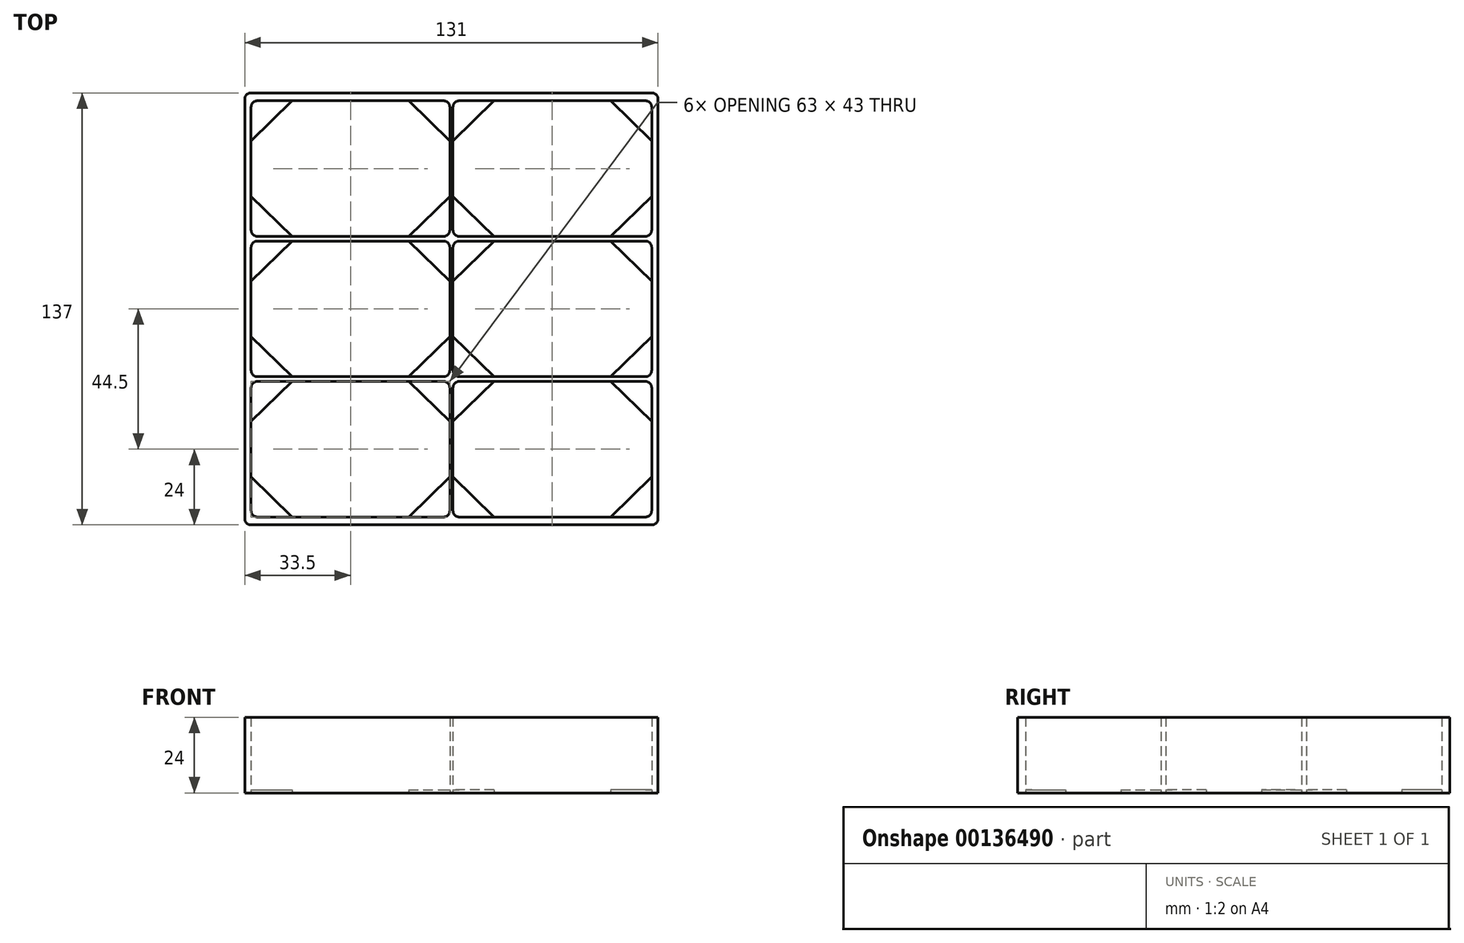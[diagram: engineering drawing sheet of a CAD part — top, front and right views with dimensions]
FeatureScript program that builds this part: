
annotation { "Feature Type Name" : "Feature", "Feature Type Description" : "" }
export const myFeature = defineFeature(function(context is Context, id is Id, definition is map)
    precondition{}
    {
        {
            var Q0;
            Q0=qCreatedBy(makeId("Top.planeOp"),FACE);
            var sketch = newSketch(context, id + "F0", { "sketchPlane" : qUnion([Q0])});
            skLineSegment(sketch, "E0.bottom", {"start": v(65.5, 68.5) * mm, "end": v(-65.5, 68.5) * mm});
            skLineSegment(sketch, "E0.top", {"start": v(65.5, -68.5) * mm, "end": v(-65.5, -68.5) * mm});
            skLineSegment(sketch, "E0.left", {"start": v(65.5, 68.5) * mm, "end": v(65.5, -68.5) * mm});
            skLineSegment(sketch, "E0.right", {"start": v(-65.5, 68.5) * mm, "end": v(-65.5, -68.5) * mm});
            skPoint(sketch, "E0.middle", {"position": v(0, 0) * mm});
            skLineSegment(sketch, "E1.bottom", {"start": v(63.5, -66) * mm, "end": v(-63.5, -66) * mm});
            skLineSegment(sketch, "E1.top", {"start": v(63.5, 66) * mm, "end": v(-63.5, 66) * mm});
            skLineSegment(sketch, "E1.left", {"start": v(63.5, -66) * mm, "end": v(63.5, 66) * mm});
            skLineSegment(sketch, "E1.right", {"start": v(-63.5, -66) * mm, "end": v(-63.5, 66) * mm});
            skLineSegment(sketch, "E2", {"start": v(-0.5, 66) * mm, "end": v(-0.5, -66) * mm});
            skPoint(sketch, "E2.endSnap0", {"position": v(0, -66) * mm});
            skLineSegment(sketch, "E3", {"start": v(-63.5, 23) * mm, "end": v(-0.5, 23) * mm});
            skLineSegment(sketch, "E4", {"start": v(-0.5, 21.5) * mm, "end": v(-63.5, 21.5) * mm});
            skLineSegment(sketch, "E5.MirrorCS", {"start": v(-63.5, -23) * mm, "end": v(-0.5, -23) * mm});
            skLineSegment(sketch, "E6.MirrorCS", {"start": v(-0.5, -21.5) * mm, "end": v(-63.5, -21.5) * mm});
            skLineSegment(sketch, "E7.MirrorCS", {"start": v(0.5, 66) * mm, "end": v(0.5, -66) * mm});
            skLineSegment(sketch, "E8.MirrorCS", {"start": v(63.5, 23) * mm, "end": v(0.5, 23) * mm});
            skLineSegment(sketch, "E9.MirrorCS", {"start": v(0.5, 21.5) * mm, "end": v(63.5, 21.5) * mm});
            skLineSegment(sketch, "E10.MirrorCS", {"start": v(0.5, -21.5) * mm, "end": v(63.5, -21.5) * mm});
            skLineSegment(sketch, "E11.MirrorCS", {"start": v(63.5, -23) * mm, "end": v(0.5, -23) * mm});
            skLineSegment(sketch, "E12", {"start": v(-63.5, 53.26) * mm, "end": v(-50.5, 66) * mm});
            skLineSegment(sketch, "E13.MirrorCS", {"start": v(63.5, 53.26) * mm, "end": v(50.5, 66) * mm});
            skLineSegment(sketch, "E14.MirrorCS", {"start": v(-63.5, -53.26) * mm, "end": v(-50.5, -66) * mm});
            skLineSegment(sketch, "E15.MirrorCS", {"start": v(63.5, -53.26) * mm, "end": v(50.5, -66) * mm});
            skLineSegment(sketch, "E16", {"start": v(-13.5, 66) * mm, "end": v(-0.5, 53.26) * mm});
            skLineSegment(sketch, "E17.MirrorCS", {"start": v(13.5, 66) * mm, "end": v(0.5, 53.26) * mm});
            skLineSegment(sketch, "E18.MirrorCS", {"start": v(-13.5, -66) * mm, "end": v(-0.5, -53.26) * mm});
            skLineSegment(sketch, "E19.MirrorCS", {"start": v(13.5, -66) * mm, "end": v(0.5, -53.26) * mm});
            skLineSegment(sketch, "E20", {"start": v(-63.5, 44.5) * mm, "end": v(63.5, 44.5) * mm, "construction": true});
            skLineSegment(sketch, "E21.MirrorCS", {"start": v(-13.5, 23) * mm, "end": v(-0.5, 35.74) * mm});
            skLineSegment(sketch, "E22.MirrorCS", {"start": v(-63.5, 35.74) * mm, "end": v(-50.5, 23) * mm});
            skLineSegment(sketch, "E23.MirrorCS", {"start": v(13.5, 23) * mm, "end": v(0.5, 35.74) * mm});
            skLineSegment(sketch, "E24.MirrorCS", {"start": v(63.5, 35.74) * mm, "end": v(50.5, 23) * mm});
            skLineSegment(sketch, "E25", {"start": v(63.5, 22.25) * mm, "end": v(-63.5, 22.25) * mm, "construction": true});
            skLineSegment(sketch, "E26.MirrorCS", {"start": v(-63.5, 8.76) * mm, "end": v(-50.5, 21.5) * mm});
            skLineSegment(sketch, "E27.MirrorCS", {"start": v(-63.5, -8.76) * mm, "end": v(-50.5, -21.5) * mm});
            skLineSegment(sketch, "E28.MirrorCS", {"start": v(-13.5, -21.5) * mm, "end": v(-0.5, -8.76) * mm});
            skLineSegment(sketch, "E29.MirrorCS", {"start": v(-13.5, 21.5) * mm, "end": v(-0.5, 8.76) * mm});
            skLineSegment(sketch, "E30.MirrorCS", {"start": v(13.5, 21.5) * mm, "end": v(0.5, 8.76) * mm});
            skLineSegment(sketch, "E31.MirrorCS", {"start": v(13.5, -21.5) * mm, "end": v(0.5, -8.76) * mm});
            skLineSegment(sketch, "E32.MirrorCS", {"start": v(63.5, -8.76) * mm, "end": v(50.5, -21.5) * mm});
            skLineSegment(sketch, "E33.MirrorCS", {"start": v(63.5, 8.76) * mm, "end": v(50.5, 21.5) * mm});
            skLineSegment(sketch, "E34.MirrorCS", {"start": v(-13.5, -23) * mm, "end": v(-0.5, -35.74) * mm});
            skLineSegment(sketch, "E35.MirrorCS", {"start": v(-63.5, -35.74) * mm, "end": v(-50.5, -23) * mm});
            skLineSegment(sketch, "E36.MirrorCS", {"start": v(13.5, -23) * mm, "end": v(0.5, -35.74) * mm});
            skLineSegment(sketch, "E37.MirrorCS", {"start": v(63.5, -35.74) * mm, "end": v(50.5, -23) * mm});
            skSolve(sketch);
        }
        {
            var Q0;
            Q0=makeQuery(id+"F0.imprint","IMPRINT",FACE,{"disambiguationData":[TD([[makeQuery(id+"F0.imprint","IMPRINT",EDGE,{"derivedFrom":sQuery(id+"F0.wireOp",EDGE,"E0.bottom")}),1.0]])]});
            var Q1;
            {var subQ12=sQuery(id+"F0.wireOp",EDGE,"E2");var subQ20=sQuery(id+"F0.wireOp",EDGE,"E1.bottom");var subQ21=makeQuery(id+"F0.imprint","INTERSECT",VERTEX,{"derivedFrom":[subQ20,subQ12]});Q1=makeQuery(id+"F0.imprint","IMPRINT",FACE,{"disambiguationData":[TD([[makeQuery(id+"F0.imprint","IMPRINT",EDGE,{"disambiguationData":[TD([[subQ21,1.0]])],"derivedFrom":subQ20}),-1.0]])]});}
            var Q2;
            {var subQ0=sQuery(id+"F0.wireOp",EDGE,"E8.MirrorCS");var subQ3=sQuery(id+"F0.wireOp",EDGE,"E1.left");var subQ4=makeQuery(id+"F0.imprint","INTERSECT",VERTEX,{"derivedFrom":[subQ3,subQ0]});Q2=makeQuery(id+"F0.imprint","IMPRINT",FACE,{"disambiguationData":[TD([[makeQuery(id+"F0.imprint","IMPRINT",EDGE,{"disambiguationData":[TD([[subQ4,1.0]])],"derivedFrom":subQ3}),1.0]])]});}
            var Q3;
            {var subQ0=sQuery(id+"F0.wireOp",EDGE,"E3");var subQ5=sQuery(id+"F0.wireOp",EDGE,"E1.right");var subQ6=makeQuery(id+"F0.imprint","INTERSECT",VERTEX,{"derivedFrom":[subQ5,subQ0]});Q3=makeQuery(id+"F0.imprint","IMPRINT",FACE,{"disambiguationData":[TD([[makeQuery(id+"F0.imprint","IMPRINT",EDGE,{"disambiguationData":[TD([[subQ6,1.0]])],"derivedFrom":subQ5}),-1.0]])]});}
            var Q4;
            {var subQ0=sQuery(id+"F0.wireOp",EDGE,"E5.MirrorCS");var subQ3=sQuery(id+"F0.wireOp",EDGE,"E1.right");var subQ4=makeQuery(id+"F0.imprint","INTERSECT",VERTEX,{"derivedFrom":[subQ3,subQ0]});Q4=makeQuery(id+"F0.imprint","IMPRINT",FACE,{"disambiguationData":[TD([[makeQuery(id+"F0.imprint","IMPRINT",EDGE,{"disambiguationData":[TD([[subQ4,-1.0]])],"derivedFrom":subQ3}),-1.0]])]});}
            var Q5;
            {var subQ0=sQuery(id+"F0.wireOp",EDGE,"E10.MirrorCS");var subQ7=sQuery(id+"F0.wireOp",EDGE,"E1.left");var subQ8=makeQuery(id+"F0.imprint","INTERSECT",VERTEX,{"derivedFrom":[subQ7,subQ0]});Q5=makeQuery(id+"F0.imprint","IMPRINT",FACE,{"disambiguationData":[TD([[makeQuery(id+"F0.imprint","IMPRINT",EDGE,{"disambiguationData":[TD([[subQ8,1.0]])],"derivedFrom":subQ7}),1.0]])]});}
            extrude(context, id + "F1", {"entities" : qUnion([Q0, Q1, Q2, Q3, Q4, Q5]), "depth" : 24 * mm});
        }
        {
            var Q0;
            {var subQ3=sQuery(id+"F0.wireOp",EDGE,"E12");Q0=makeQuery(id+"F0.imprint","IMPRINT",FACE,{"disambiguationData":[TD([[makeQuery(id+"F0.imprint","IMPRINT",EDGE,{"derivedFrom":subQ3}),1.0]])]});}
            var Q1;
            {var subQ3=sQuery(id+"F0.wireOp",EDGE,"E22.MirrorCS");Q1=makeQuery(id+"F0.imprint","IMPRINT",FACE,{"disambiguationData":[TD([[makeQuery(id+"F0.imprint","IMPRINT",EDGE,{"derivedFrom":subQ3}),-1.0]])]});}
            var Q2;
            {var subQ3=sQuery(id+"F0.wireOp",EDGE,"E16");Q2=makeQuery(id+"F0.imprint","IMPRINT",FACE,{"disambiguationData":[TD([[makeQuery(id+"F0.imprint","IMPRINT",EDGE,{"derivedFrom":subQ3}),1.0]])]});}
            var Q3;
            {var subQ3=sQuery(id+"F0.wireOp",EDGE,"E21.MirrorCS");Q3=makeQuery(id+"F0.imprint","IMPRINT",FACE,{"disambiguationData":[TD([[makeQuery(id+"F0.imprint","IMPRINT",EDGE,{"derivedFrom":subQ3}),-1.0]])]});}
            var Q4;
            {var subQ3=sQuery(id+"F0.wireOp",EDGE,"E17.MirrorCS");Q4=makeQuery(id+"F0.imprint","IMPRINT",FACE,{"disambiguationData":[TD([[makeQuery(id+"F0.imprint","IMPRINT",EDGE,{"derivedFrom":subQ3}),-1.0]])]});}
            var Q5;
            {var subQ3=sQuery(id+"F0.wireOp",EDGE,"E13.MirrorCS");Q5=makeQuery(id+"F0.imprint","IMPRINT",FACE,{"disambiguationData":[TD([[makeQuery(id+"F0.imprint","IMPRINT",EDGE,{"derivedFrom":subQ3}),-1.0]])]});}
            var Q6;
            {var subQ3=sQuery(id+"F0.wireOp",EDGE,"E24.MirrorCS");Q6=makeQuery(id+"F0.imprint","IMPRINT",FACE,{"disambiguationData":[TD([[makeQuery(id+"F0.imprint","IMPRINT",EDGE,{"derivedFrom":subQ3}),1.0]])]});}
            var Q7;
            {var subQ3=sQuery(id+"F0.wireOp",EDGE,"E23.MirrorCS");Q7=makeQuery(id+"F0.imprint","IMPRINT",FACE,{"disambiguationData":[TD([[makeQuery(id+"F0.imprint","IMPRINT",EDGE,{"derivedFrom":subQ3}),1.0]])]});}
            var Q8;
            {var subQ3=sQuery(id+"F0.wireOp",EDGE,"E30.MirrorCS");Q8=makeQuery(id+"F0.imprint","IMPRINT",FACE,{"disambiguationData":[TD([[makeQuery(id+"F0.imprint","IMPRINT",EDGE,{"derivedFrom":subQ3}),-1.0]])]});}
            var Q9;
            {var subQ3=sQuery(id+"F0.wireOp",EDGE,"E29.MirrorCS");Q9=makeQuery(id+"F0.imprint","IMPRINT",FACE,{"disambiguationData":[TD([[makeQuery(id+"F0.imprint","IMPRINT",EDGE,{"derivedFrom":subQ3}),1.0]])]});}
            var Q10;
            {var subQ3=sQuery(id+"F0.wireOp",EDGE,"E26.MirrorCS");Q10=makeQuery(id+"F0.imprint","IMPRINT",FACE,{"disambiguationData":[TD([[makeQuery(id+"F0.imprint","IMPRINT",EDGE,{"derivedFrom":subQ3}),1.0]])]});}
            var Q11;
            {var subQ3=sQuery(id+"F0.wireOp",EDGE,"E27.MirrorCS");Q11=makeQuery(id+"F0.imprint","IMPRINT",FACE,{"disambiguationData":[TD([[makeQuery(id+"F0.imprint","IMPRINT",EDGE,{"derivedFrom":subQ3}),-1.0]])]});}
            var Q12;
            {var subQ3=sQuery(id+"F0.wireOp",EDGE,"E28.MirrorCS");Q12=makeQuery(id+"F0.imprint","IMPRINT",FACE,{"disambiguationData":[TD([[makeQuery(id+"F0.imprint","IMPRINT",EDGE,{"derivedFrom":subQ3}),-1.0]])]});}
            var Q13;
            {var subQ3=sQuery(id+"F0.wireOp",EDGE,"E32.MirrorCS");Q13=makeQuery(id+"F0.imprint","IMPRINT",FACE,{"disambiguationData":[TD([[makeQuery(id+"F0.imprint","IMPRINT",EDGE,{"derivedFrom":subQ3}),1.0]])]});}
            var Q14;
            {var subQ3=sQuery(id+"F0.wireOp",EDGE,"E33.MirrorCS");Q14=makeQuery(id+"F0.imprint","IMPRINT",FACE,{"disambiguationData":[TD([[makeQuery(id+"F0.imprint","IMPRINT",EDGE,{"derivedFrom":subQ3}),-1.0]])]});}
            var Q15;
            {var subQ3=sQuery(id+"F0.wireOp",EDGE,"E31.MirrorCS");Q15=makeQuery(id+"F0.imprint","IMPRINT",FACE,{"disambiguationData":[TD([[makeQuery(id+"F0.imprint","IMPRINT",EDGE,{"derivedFrom":subQ3}),1.0]])]});}
            var Q16;
            {var subQ3=sQuery(id+"F0.wireOp",EDGE,"E36.MirrorCS");Q16=makeQuery(id+"F0.imprint","IMPRINT",FACE,{"disambiguationData":[TD([[makeQuery(id+"F0.imprint","IMPRINT",EDGE,{"derivedFrom":subQ3}),-1.0]])]});}
            var Q17;
            {var subQ3=sQuery(id+"F0.wireOp",EDGE,"E34.MirrorCS");Q17=makeQuery(id+"F0.imprint","IMPRINT",FACE,{"disambiguationData":[TD([[makeQuery(id+"F0.imprint","IMPRINT",EDGE,{"derivedFrom":subQ3}),1.0]])]});}
            var Q18;
            {var subQ3=sQuery(id+"F0.wireOp",EDGE,"E35.MirrorCS");Q18=makeQuery(id+"F0.imprint","IMPRINT",FACE,{"disambiguationData":[TD([[makeQuery(id+"F0.imprint","IMPRINT",EDGE,{"derivedFrom":subQ3}),1.0]])]});}
            var Q19;
            {var subQ3=sQuery(id+"F0.wireOp",EDGE,"E14.MirrorCS");Q19=makeQuery(id+"F0.imprint","IMPRINT",FACE,{"disambiguationData":[TD([[makeQuery(id+"F0.imprint","IMPRINT",EDGE,{"derivedFrom":subQ3}),-1.0]])]});}
            var Q20;
            {var subQ3=sQuery(id+"F0.wireOp",EDGE,"E18.MirrorCS");Q20=makeQuery(id+"F0.imprint","IMPRINT",FACE,{"disambiguationData":[TD([[makeQuery(id+"F0.imprint","IMPRINT",EDGE,{"derivedFrom":subQ3}),-1.0]])]});}
            var Q21;
            {var subQ3=sQuery(id+"F0.wireOp",EDGE,"E19.MirrorCS");Q21=makeQuery(id+"F0.imprint","IMPRINT",FACE,{"disambiguationData":[TD([[makeQuery(id+"F0.imprint","IMPRINT",EDGE,{"derivedFrom":subQ3}),1.0]])]});}
            var Q22;
            {var subQ3=sQuery(id+"F0.wireOp",EDGE,"E37.MirrorCS");Q22=makeQuery(id+"F0.imprint","IMPRINT",FACE,{"disambiguationData":[TD([[makeQuery(id+"F0.imprint","IMPRINT",EDGE,{"derivedFrom":subQ3}),-1.0]])]});}
            var Q23;
            {var subQ3=sQuery(id+"F0.wireOp",EDGE,"E15.MirrorCS");Q23=makeQuery(id+"F0.imprint","IMPRINT",FACE,{"disambiguationData":[TD([[makeQuery(id+"F0.imprint","IMPRINT",EDGE,{"derivedFrom":subQ3}),1.0]])]});}
            extrude(context, id + "F2", {"entities" : qUnion([Q0, Q1, Q2, Q3, Q4, Q5, Q6, Q7, Q8, Q9, Q10, Q11, Q12, Q13, Q14, Q15, Q16, Q17, Q18, Q19, Q20, Q21, Q22, Q23]), "operationType" : NewBodyOperationType.ADD, "depth" : 1 * mm});
        }
        {
            var Q0;
            Q0=makeQuery(id+"F1.opExtrude","SWEPT_EDGE",EDGE,{"disambiguationData":[OSD([sQuery(id+"F0.wireOp",EDGE,"E0.bottom"),sQuery(id+"F0.wireOp",EDGE,"E0.right")])]});
            var Q1;
            Q1=makeQuery(id+"F1.opExtrude","SWEPT_EDGE",EDGE,{"disambiguationData":[OSD([sQuery(id+"F0.wireOp",EDGE,"E0.bottom"),sQuery(id+"F0.wireOp",EDGE,"E0.left")])]});
            var Q2;
            Q2=makeQuery(id+"F1.opExtrude","SWEPT_EDGE",EDGE,{"disambiguationData":[OSD([sQuery(id+"F0.wireOp",EDGE,"E0.top"),sQuery(id+"F0.wireOp",EDGE,"E0.right")])]});
            var Q3;
            Q3=makeQuery(id+"F1.opExtrude","SWEPT_EDGE",EDGE,{"disambiguationData":[OSD([sQuery(id+"F0.wireOp",EDGE,"E0.top"),sQuery(id+"F0.wireOp",EDGE,"E0.left")])]});
            var Q4;
            Q4=makeQuery(id+"F1.opExtrude","SWEPT_EDGE",EDGE,{"disambiguationData":[OSD([sQuery(id+"F0.wireOp",EDGE,"E1.left"),sQuery(id+"F0.wireOp",EDGE,"E11.MirrorCS")])]});
            var Q5;
            Q5=makeQuery(id+"F1.opExtrude","SWEPT_EDGE",EDGE,{"disambiguationData":[OSD([sQuery(id+"F0.wireOp",EDGE,"E1.top"),sQuery(id+"F0.wireOp",EDGE,"E1.left")])]});
            var Q6;
            Q6=makeQuery(id+"F1.opExtrude","SWEPT_EDGE",EDGE,{"disambiguationData":[OSD([sQuery(id+"F0.wireOp",EDGE,"E1.top"),sQuery(id+"F0.wireOp",EDGE,"E2")])]});
            var Q7;
            Q7=makeQuery(id+"F1.opExtrude","SWEPT_EDGE",EDGE,{"disambiguationData":[OSD([sQuery(id+"F0.wireOp",EDGE,"E2"),sQuery(id+"F0.wireOp",EDGE,"E4")])]});
            var Q8;
            Q8=makeQuery(id+"F1.opExtrude","SWEPT_EDGE",EDGE,{"disambiguationData":[OSD([sQuery(id+"F0.wireOp",EDGE,"E2"),sQuery(id+"F0.wireOp",EDGE,"E5.MirrorCS")])]});
            var Q9;
            Q9=makeQuery(id+"F1.opExtrude","SWEPT_EDGE",EDGE,{"disambiguationData":[OSD([sQuery(id+"F0.wireOp",EDGE,"E1.left"),sQuery(id+"F0.wireOp",EDGE,"E9.MirrorCS")])]});
            var Q10;
            Q10=makeQuery(id+"F1.opExtrude","SWEPT_EDGE",EDGE,{"disambiguationData":[OSD([sQuery(id+"F0.wireOp",EDGE,"E1.right"),sQuery(id+"F0.wireOp",EDGE,"E4")])]});
            var Q11;
            Q11=makeQuery(id+"F1.opExtrude","SWEPT_EDGE",EDGE,{"disambiguationData":[OSD([sQuery(id+"F0.wireOp",EDGE,"E1.top"),sQuery(id+"F0.wireOp",EDGE,"E1.right")])]});
            var Q12;
            Q12=makeQuery(id+"F1.opExtrude","SWEPT_EDGE",EDGE,{"disambiguationData":[OSD([sQuery(id+"F0.wireOp",EDGE,"E1.right"),sQuery(id+"F0.wireOp",EDGE,"E5.MirrorCS")])]});
            var Q13;
            Q13=makeQuery(id+"F1.opExtrude","SWEPT_EDGE",EDGE,{"disambiguationData":[OSD([sQuery(id+"F0.wireOp",EDGE,"E1.top"),sQuery(id+"F0.wireOp",EDGE,"E7.MirrorCS")])]});
            var Q14;
            Q14=makeQuery(id+"F1.opExtrude","SWEPT_EDGE",EDGE,{"disambiguationData":[OSD([sQuery(id+"F0.wireOp",EDGE,"E7.MirrorCS"),sQuery(id+"F0.wireOp",EDGE,"E9.MirrorCS")])]});
            var Q15;
            Q15=makeQuery(id+"F1.opExtrude","SWEPT_EDGE",EDGE,{"disambiguationData":[OSD([sQuery(id+"F0.wireOp",EDGE,"E7.MirrorCS"),sQuery(id+"F0.wireOp",EDGE,"E11.MirrorCS")])]});
            var Q16;
            Q16=makeQuery(id+"F1.opExtrude","SWEPT_EDGE",EDGE,{"disambiguationData":[OSD([sQuery(id+"F0.wireOp",EDGE,"E1.bottom"),sQuery(id+"F0.wireOp",EDGE,"E1.right")])]});
            var Q17;
            Q17=makeQuery(id+"F1.opExtrude","SWEPT_EDGE",EDGE,{"disambiguationData":[OSD([sQuery(id+"F0.wireOp",EDGE,"E1.right"),sQuery(id+"F0.wireOp",EDGE,"E6.MirrorCS")])]});
            var Q18;
            Q18=makeQuery(id+"F1.opExtrude","SWEPT_EDGE",EDGE,{"disambiguationData":[OSD([sQuery(id+"F0.wireOp",EDGE,"E1.right"),sQuery(id+"F0.wireOp",EDGE,"E3")])]});
            var Q19;
            Q19=makeQuery(id+"F1.opExtrude","SWEPT_EDGE",EDGE,{"disambiguationData":[OSD([sQuery(id+"F0.wireOp",EDGE,"E7.MirrorCS"),sQuery(id+"F0.wireOp",EDGE,"E8.MirrorCS")])]});
            var Q20;
            Q20=makeQuery(id+"F1.opExtrude","SWEPT_EDGE",EDGE,{"disambiguationData":[OSD([sQuery(id+"F0.wireOp",EDGE,"E7.MirrorCS"),sQuery(id+"F0.wireOp",EDGE,"E10.MirrorCS")])]});
            var Q21;
            Q21=makeQuery(id+"F1.opExtrude","SWEPT_EDGE",EDGE,{"disambiguationData":[OSD([sQuery(id+"F0.wireOp",EDGE,"E1.bottom"),sQuery(id+"F0.wireOp",EDGE,"E7.MirrorCS")])]});
            var Q22;
            Q22=makeQuery(id+"F1.opExtrude","SWEPT_EDGE",EDGE,{"disambiguationData":[OSD([sQuery(id+"F0.wireOp",EDGE,"E1.bottom"),sQuery(id+"F0.wireOp",EDGE,"E2")])]});
            var Q23;
            Q23=makeQuery(id+"F1.opExtrude","SWEPT_EDGE",EDGE,{"disambiguationData":[OSD([sQuery(id+"F0.wireOp",EDGE,"E2"),sQuery(id+"F0.wireOp",EDGE,"E6.MirrorCS")])]});
            var Q24;
            Q24=makeQuery(id+"F1.opExtrude","SWEPT_EDGE",EDGE,{"disambiguationData":[OSD([sQuery(id+"F0.wireOp",EDGE,"E2"),sQuery(id+"F0.wireOp",EDGE,"E3")])]});
            var Q25;
            Q25=makeQuery(id+"F1.opExtrude","SWEPT_EDGE",EDGE,{"disambiguationData":[OSD([sQuery(id+"F0.wireOp",EDGE,"E1.left"),sQuery(id+"F0.wireOp",EDGE,"E8.MirrorCS")])]});
            var Q26;
            Q26=makeQuery(id+"F1.opExtrude","SWEPT_EDGE",EDGE,{"disambiguationData":[OSD([sQuery(id+"F0.wireOp",EDGE,"E1.left"),sQuery(id+"F0.wireOp",EDGE,"E10.MirrorCS")])]});
            var Q27;
            Q27=makeQuery(id+"F1.opExtrude","SWEPT_EDGE",EDGE,{"disambiguationData":[OSD([sQuery(id+"F0.wireOp",EDGE,"E1.bottom"),sQuery(id+"F0.wireOp",EDGE,"E1.left")])]});
            fillet(context, id + "F3", {"entities" : qUnion([Q0, Q1, Q2, Q3, Q4, Q5, Q6, Q7, Q8, Q9, Q10, Q11, Q12, Q13, Q14, Q15, Q16, Q17, Q18, Q19, Q20, Q21, Q22, Q23, Q24, Q25, Q26, Q27]), "radius" : 2 * mm, "tangentPropagation" : true, "allowEdgeOverflow" : false});
        }
    });
